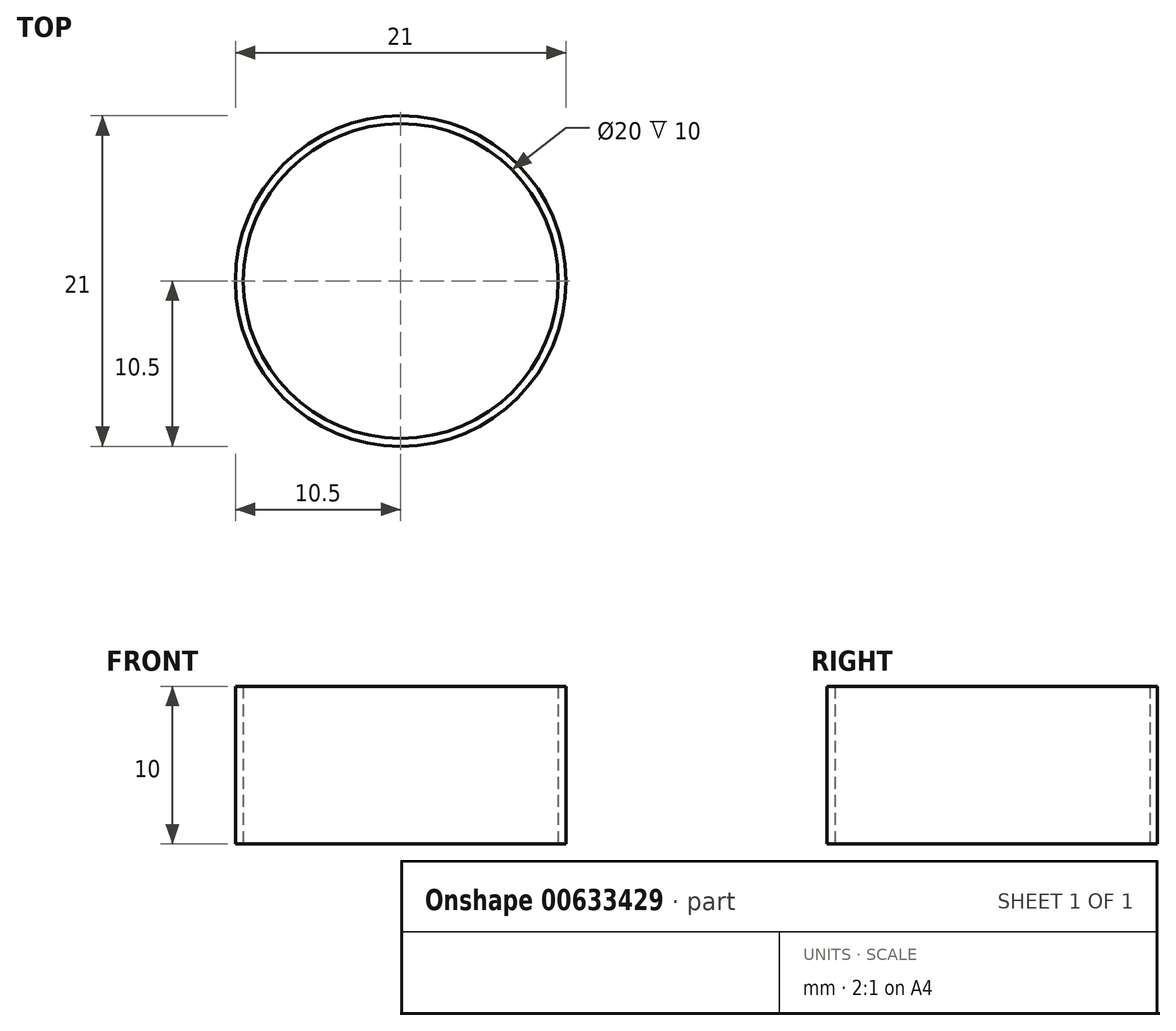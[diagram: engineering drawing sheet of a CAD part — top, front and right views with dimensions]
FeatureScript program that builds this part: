
annotation { "Feature Type Name" : "Feature", "Feature Type Description" : "" }
export const myFeature = defineFeature(function(context is Context, id is Id, definition is map)
    precondition{}
    {
        {
            var Q0;
            Q0=qCreatedBy(makeId("Top.planeOp"),FACE);
            var sketch = newSketch(context, id + "F0", { "sketchPlane" : qUnion([Q0])});
            skCircle(sketch, "E0", {"center": v(0, 0) * mm, "radius": 10.5 * mm});
            skCircle(sketch, "E1", {"center": v(0, 0) * mm, "radius": 10 * mm});
            skSolve(sketch);
        }
        {
            var Q0;
            Q0 = qSketchRegion(id + "F0", true);
            extrude(context, id + "F1", {"entities" : qUnion([Q0]), "depth" : 10 * mm, "offsetDistance" : 25 * mm});
        }
    });
